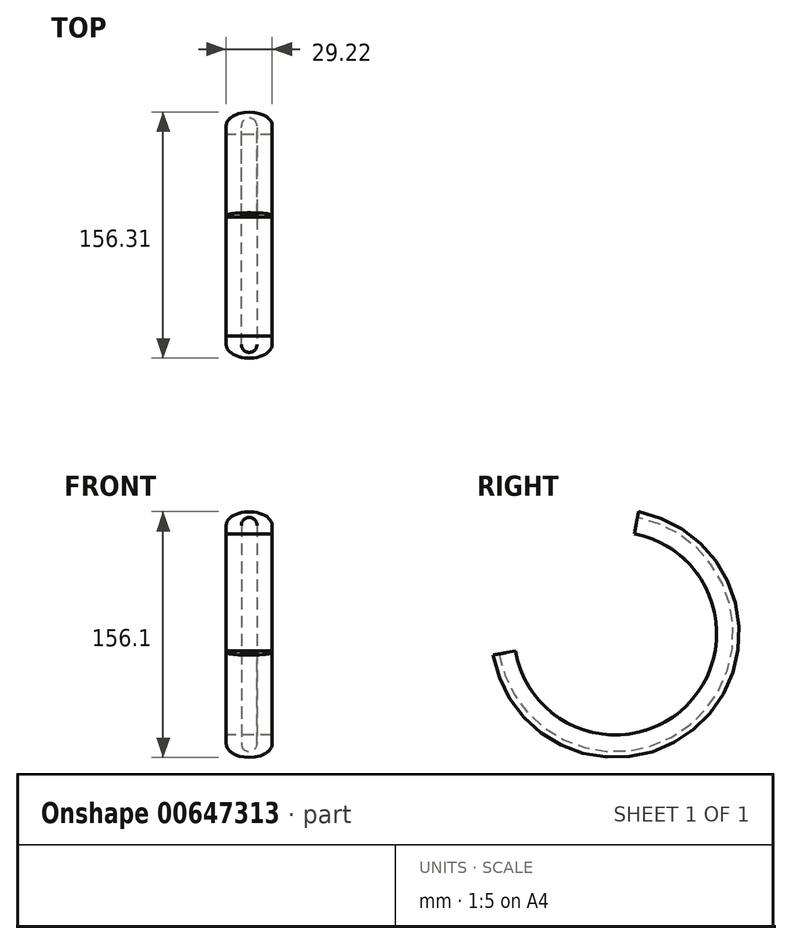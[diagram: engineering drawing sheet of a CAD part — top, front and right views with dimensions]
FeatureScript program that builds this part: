
annotation { "Feature Type Name" : "Feature", "Feature Type Description" : "" }
export const myFeature = defineFeature(function(context is Context, id is Id, definition is map)
    precondition{}
    {
        {
            var Q0;
            Q0=qCreatedBy(makeId("Top.planeOp"),FACE);
            var sketch = newSketch(context, id + "F0", { "sketchPlane" : qUnion([Q0])});
            skArc(sketch, "E0", {"start": v(-5, 0) * mm, "mid": v(0, -5) * mm, "end": v(5, 0) * mm, "construction": true});
            skLineSegment(sketch, "E1", {"start": v(0, -11.06) * mm, "end": v(-27.42, 0) * mm, "construction": true});
            skLineSegment(sketch, "E2", {"start": v(-27.42, 0) * mm, "end": v(27.62, 0) * mm, "construction": true});
            skLineSegment(sketch, "E3", {"start": v(0, 13.61) * mm, "end": v(0, -11.06) * mm, "construction": true});
            skEllipticalArc(sketch, "E4", {});
            skCircle(sketch, "E5", {"center": v(0, 0) * mm, "radius": 5 * mm});
            skEllipticalArc(sketch, "E6.MirrorCS", {});
            skLineSegment(sketch, "E7", {"start": v(-14.6, 0) * mm, "end": v(14.6, 0) * mm});
            skLineSegment(sketch, "E8.top", {"start": v(-14.6, -5.57) * mm, "end": v(14.6, -5.57) * mm});
            skLineSegment(sketch, "E8.left", {"start": v(-14.6, 0) * mm, "end": v(-14.6, -5.57) * mm});
            skLineSegment(sketch, "E8.right", {"start": v(14.6, 0) * mm, "end": v(14.6, -5.57) * mm});
            const initialGuessF0  = {"E4": [0, 0, 1, 0, 0.014606086537241936, 0.008753913454711437, 1.5707963267948966, 3.141592653589793], "E6.MirrorCS": [0, 0, -1, 0, 0.014606086537241936, 0.008753913454711437, 3.141592653589793, 4.71238898038469]};
            skSetInitialGuess(sketch, initialGuessF0);
            skSolve(sketch);
        }
        {
            var Q0;
            Q0=qCreatedBy(makeId("Right.planeOp"),FACE);
            var sketch = newSketch(context, id + "F1", { "sketchPlane" : qUnion([Q0])});
            skArc(sketch, "E9", {"start": v(0, 0) * mm, "mid": v(-119.5, 49.5) * mm, "end": v(-70, -70) * mm});
            skSolve(sketch);
        }
        {
            var Q0;
            Q0=qCreatedBy(makeId("Right.planeOp"),FACE);
            var sketch = newSketch(context, id + "F2", { "sketchPlane" : qUnion([Q0])});
            skArc(sketch, "E10", {"start": v(-1.06, 12.16) * mm, "mid": v(-119.13, 49.86) * mm, "end": v(-83.18, -68.75) * mm});
            skSolve(sketch);
        }
        {
            var Q0;
            Q0 = qSketchRegion(id + "F0", true);
            var Q1;
            Q1=sQuery(id+"F0.wireOp",EDGE,"E6.MirrorCS");
            var Q2;
            Q2=sQuery(id+"F0.wireOp",EDGE,"E4");
            var Q3;
            Q3=sQuery(id+"F0.wireOp",EDGE,"E8.left");
            var Q4;
            Q4=sQuery(id+"F0.wireOp",EDGE,"E8.top");
            var Q5;
            Q5=sQuery(id+"F0.wireOp",EDGE,"E8.right");
            var Q6;
            Q6=sQuery(id+"F0.wireOp",EDGE,"E5");
            var Q7;
            Q7 = qConstructionFilter(qBodyType(qCreatedBy(id + "F2" ,EDGE), BodyType.WIRE), ConstructionObject.NO);
            sweep(context, id + "F3", {"profiles" : qUnion([Q0]), "surfaceProfiles" : qUnion([Q1, Q2, Q3, Q4, Q5, Q6]), "path" : qUnion([Q7])});
        }
    });
